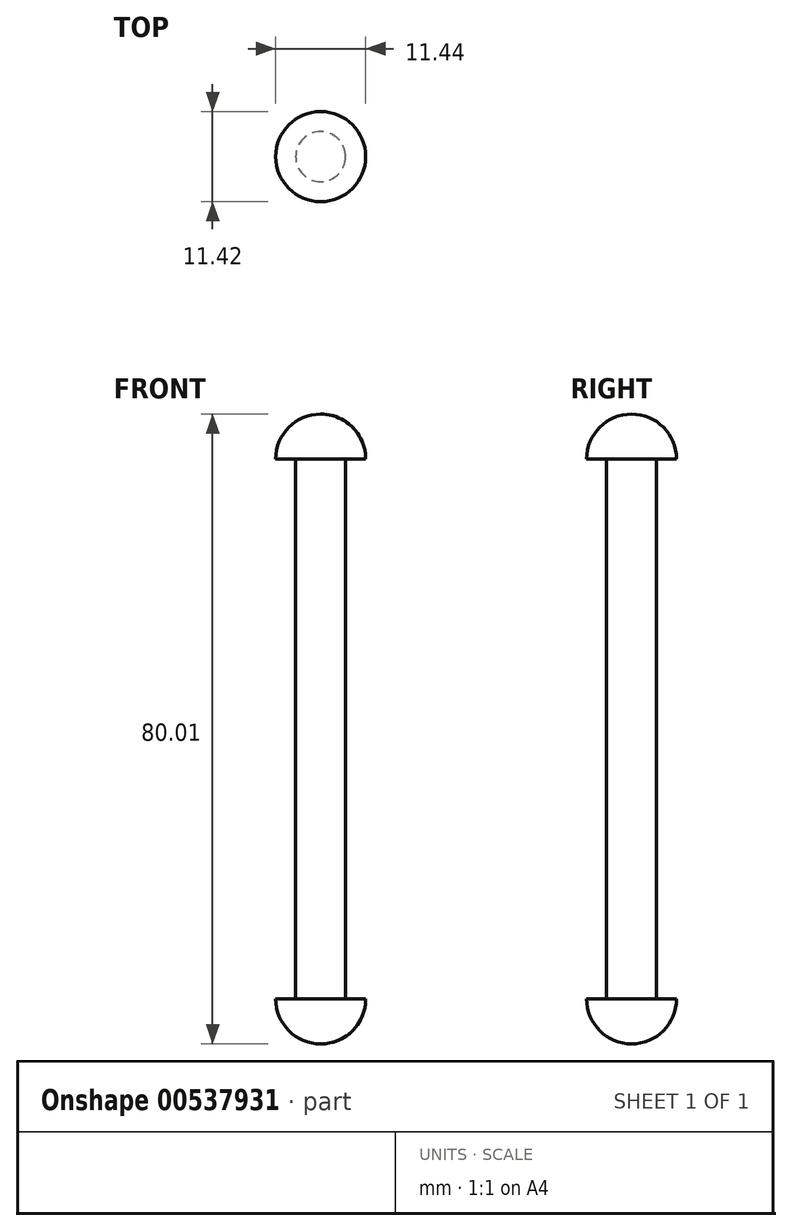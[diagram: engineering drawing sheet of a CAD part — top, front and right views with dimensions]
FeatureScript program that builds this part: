
annotation { "Feature Type Name" : "Feature", "Feature Type Description" : "" }
export const myFeature = defineFeature(function(context is Context, id is Id, definition is map)
    precondition{}
    {
        {
            var Q0;
            Q0=qCreatedBy(makeId("Front.planeOp"),FACE);
            var sketch = newSketch(context, id + "F0", { "sketchPlane" : qUnion([Q0])});
            skLineSegment(sketch, "E0", {"start": v(0, 0) * mm, "end": v(0, 80.01) * mm});
            skLineSegment(sketch, "E1", {"start": v(0, 80.01) * mm, "end": v(0, 80.01) * mm});
            skLineSegment(sketch, "E2", {"start": v(5.72, 74.3) * mm, "end": v(5.72, 74.3) * mm});
            skLineSegment(sketch, "E3", {"start": v(0, 0) * mm, "end": v(0, 0) * mm});
            skLineSegment(sketch, "E4", {"start": v(5.72, 5.72) * mm, "end": v(5.72, 5.72) * mm});
            skLineSegment(sketch, "E5.0", {"start": v(3.18, 5.72) * mm, "end": v(3.17, 74.3) * mm});
            skLineSegment(sketch, "E6", {"start": v(5.72, 5.72) * mm, "end": v(3.18, 5.72) * mm});
            skLineSegment(sketch, "E7", {"start": v(5.72, 74.3) * mm, "end": v(3.17, 74.3) * mm});
            skPoint(sketch, "E8.visualSharp", {"position": v(5.72, 0) * mm});
            skArc(sketch, "E8.filletArc", {"start": v(0, 0) * mm, "mid": v(4.04, 1.67) * mm, "end": v(5.71, 5.72) * mm});
            skPoint(sketch, "E9.visualSharp", {"position": v(5.72, 80.01) * mm});
            skArc(sketch, "E9.filletArc", {"start": v(5.72, 74.3) * mm, "mid": v(4.04, 78.34) * mm, "end": v(0, 80.01) * mm});
            skSolve(sketch);
        }
        {
            var Q0;
            Q0 = qSketchRegion(id + "F0", true);
            var Q1;
            Q1=sQuery(id+"F0.wireOp",EDGE,"E0");
            revolve(context, id + "F1", {"entities" : qUnion([Q0]), "axis" : qUnion([Q1]), "revolveType" : RevolveType.FULL});
        }
    });
